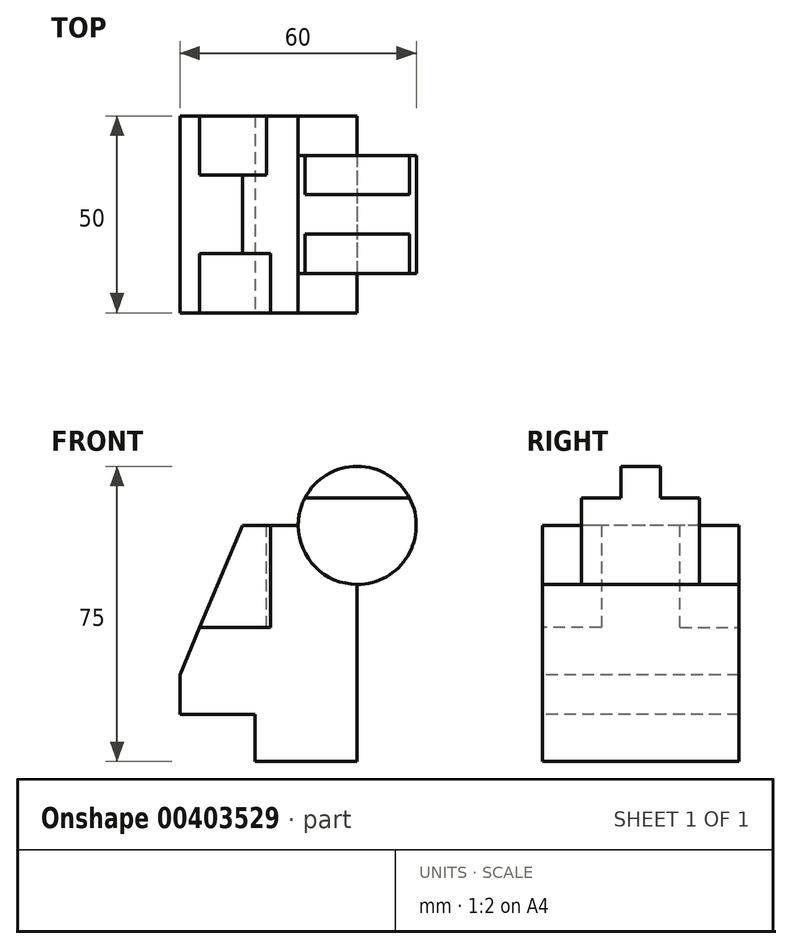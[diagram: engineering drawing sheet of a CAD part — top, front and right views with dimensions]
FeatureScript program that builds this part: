
annotation { "Feature Type Name" : "Feature", "Feature Type Description" : "" }
export const myFeature = defineFeature(function(context is Context, id is Id, definition is map)
    precondition{}
    {
        {
            var Q0;
            Q0=qCreatedBy(makeId("Front.planeOp"),FACE);
            var sketch = newSketch(context, id + "F0", { "sketchPlane" : qUnion([Q0])});
            skArc(sketch, "E0", {"start": v(-15, 0) * mm, "mid": v(-10.6, -10.6) * mm, "end": v(0, -15) * mm});
            skLineSegment(sketch, "E1", {"start": v(-15, 0) * mm, "end": v(-22, 0) * mm});
            skLineSegment(sketch, "E2", {"start": v(-22, 0) * mm, "end": v(-22, -26) * mm});
            skLineSegment(sketch, "E3", {"start": v(-22, -26) * mm, "end": v(-40, -26) * mm});
            skLineSegment(sketch, "E4", {"start": v(-40, -26) * mm, "end": v(-45, -38) * mm});
            skLineSegment(sketch, "E5", {"start": v(-45, -38) * mm, "end": v(-45, -48) * mm});
            skLineSegment(sketch, "E6", {"start": v(-45, -48) * mm, "end": v(-26, -48) * mm});
            skLineSegment(sketch, "E7", {"start": v(-26, -48) * mm, "end": v(-26, -60) * mm});
            skLineSegment(sketch, "E8", {"start": v(-26, -60) * mm, "end": v(0, -60) * mm});
            skLineSegment(sketch, "E9", {"start": v(0, 0) * mm, "end": v(0, -60) * mm, "construction": true});
            skLineSegment(sketch, "E10", {"start": v(0, -15) * mm, "end": v(0, -60) * mm});
            skSolve(sketch);
        }
        {
            var Q0;
            Q0=makeQuery(id+"F0.imprint","IMPRINT",FACE,{"disambiguationData":[TD([[makeQuery(id+"F0.imprint","IMPRINT",EDGE,{"derivedFrom":sQuery(id+"F0.wireOp",EDGE,"E0")}),-1.0]])]});
            extrude(context, id + "F1", {"entities" : qUnion([Q0]), "endBound" : BoundingType.SYMMETRIC, "oppositeDirection" : true, "depth" : 50 * mm});
        }
        {
            var Q0;
            Q0=makeQuery(id+"F1.opExtrude","SWEPT_FACE",FACE,{"disambiguationData":[OSD([sQuery(id+"F0.wireOp",EDGE,"E2")])]});
            var sketch = newSketch(context, id + "F2", { "sketchPlane" : qUnion([Q0])});
            skLineSegment(sketch, "E11.bottom", {"start": v(-10, 0) * mm, "end": v(10, 0) * mm});
            skLineSegment(sketch, "E11.top", {"start": v(-10, -26) * mm, "end": v(10, -26) * mm});
            skLineSegment(sketch, "E11.left", {"start": v(-10, 0) * mm, "end": v(-10, -26) * mm});
            skLineSegment(sketch, "E11.right", {"start": v(10, 0) * mm, "end": v(10, -26) * mm});
            skSolve(sketch);
        }
        {
            var Q0;
            Q0 = qSketchRegion(id + "F2", true);
            var Q1;
            Q1=makeQuery(id+"F1.opExtrude","SWEPT_FACE",FACE,{"disambiguationData":[OSD([sQuery(id+"F0.wireOp",EDGE,"E4")])]});
            extrude(context, id + "F3", {"entities" : qUnion([Q0]), "operationType" : NewBodyOperationType.ADD, "endBound" : BoundingType.UP_TO_SURFACE, "endBoundEntityFace" : qUnion([Q1]), "depth" : 25 * mm});
        }
        {
            var Q0;
            Q0=makeQuery(id+"F3.boolean.opBoolean","MERGE",FACE,{"derivedFrom":[makeQuery(id+"F1.opExtrude","SWEPT_FACE",FACE,{"disambiguationData":[OSD([sQuery(id+"F0.wireOp",EDGE,"E1")])]}),makeQuery(id+"F3.opExtrude","SWEPT_FACE",FACE,{"disambiguationData":[OSD([sQuery(id+"F2.wireOp",EDGE,"E11.bottom")])]})]});
            var sketch = newSketch(context, id + "F4", { "sketchPlane" : qUnion([Q0])});
            skLineSegment(sketch, "E12", {"start": v(-22, 25) * mm, "end": v(-23, 25) * mm});
            skLineSegment(sketch, "E13", {"start": v(-23, 25) * mm, "end": v(-23, 10) * mm});
            skLineSegment(sketch, "E14", {"start": v(-23, 10) * mm, "end": v(-22, 10) * mm});
            skLineSegment(sketch, "E15", {"start": v(-22, 10) * mm, "end": v(-22, 25) * mm});
            skSolve(sketch);
        }
        {
            var Q0;
            Q0 = qSketchRegion(id + "F4", true);
            var Q1;
            {var subQ2=sQuery(id+"F0.wireOp",EDGE,"E3");Q1=makeQuery(id+"F3.boolean.opBoolean","SPLIT",FACE,{"disambiguationData":[TD([makeQuery(id+"F3.opExtrude","SWEPT_FACE",FACE,{"disambiguationData":[OSD([sQuery(id+"F2.wireOp",EDGE,"E11.left")])]})])],"derivedFrom":makeQuery(id+"F1.opExtrude","SWEPT_FACE",FACE,{"disambiguationData":[OSD([subQ2])]})});}
            extrude(context, id + "F5", {"entities" : qUnion([Q0]), "operationType" : NewBodyOperationType.ADD, "endBound" : BoundingType.UP_TO_SURFACE, "oppositeDirection" : true, "endBoundEntityFace" : qUnion([Q1]), "depth" : 25 * mm});
        }
        {
            var Q0;
            Q0=qCreatedBy(makeId("Front.planeOp"),FACE);
            var sketch = newSketch(context, id + "F6", { "sketchPlane" : qUnion([Q0])});
            skCircle(sketch, "E16", {"center": v(0, 0) * mm, "radius": 15 * mm});
            skSolve(sketch);
        }
        {
            var Q0;
            Q0 = qSketchRegion(id + "F6", true);
            extrude(context, id + "F7", {"entities" : qUnion([Q0]), "operationType" : NewBodyOperationType.ADD, "endBound" : BoundingType.SYMMETRIC, "depth" : 30 * mm});
        }
        {
            var Q0;
            Q0=qCreatedBy(makeId("Top.planeOp"),FACE);
            cPlane(context, id + "F8", {"entities" : qUnion([Q0]), "cplaneType" : CPlaneType.OFFSET, "offset" : 15 * mm, "width" : 150 * mm, "height" : 150 * mm});
        }
        {
            var Q0;
            Q0=qCreatedBy(id+"F8.planeOp",FACE);
            var sketch = newSketch(context, id + "F9", { "sketchPlane" : qUnion([Q0])});
            skLineSegment(sketch, "E17.bottom", {"start": v(-14.24, 15) * mm, "end": v(13.34, 15) * mm});
            skLineSegment(sketch, "E17.top", {"start": v(-14.24, 5) * mm, "end": v(13.34, 5) * mm});
            skLineSegment(sketch, "E17.left", {"start": v(-14.24, 15) * mm, "end": v(-14.24, 5) * mm});
            skLineSegment(sketch, "E17.right", {"start": v(13.34, 15) * mm, "end": v(13.34, 5) * mm});
            skLineSegment(sketch, "E18.bottom", {"start": v(-13.8, -5) * mm, "end": v(13.34, -5) * mm});
            skLineSegment(sketch, "E18.top", {"start": v(-13.8, -15) * mm, "end": v(13.34, -15) * mm});
            skLineSegment(sketch, "E18.left", {"start": v(-13.8, -5) * mm, "end": v(-13.8, -15) * mm});
            skLineSegment(sketch, "E18.right", {"start": v(13.34, -5) * mm, "end": v(13.34, -15) * mm});
            skSolve(sketch);
        }
        {
            var Q0;
            Q0 = qSketchRegion(id + "F9", true);
            extrude(context, id + "F10", {"entities" : qUnion([Q0]), "operationType" : NewBodyOperationType.REMOVE, "oppositeDirection" : true, "depth" : 8 * mm});
        }
    });
